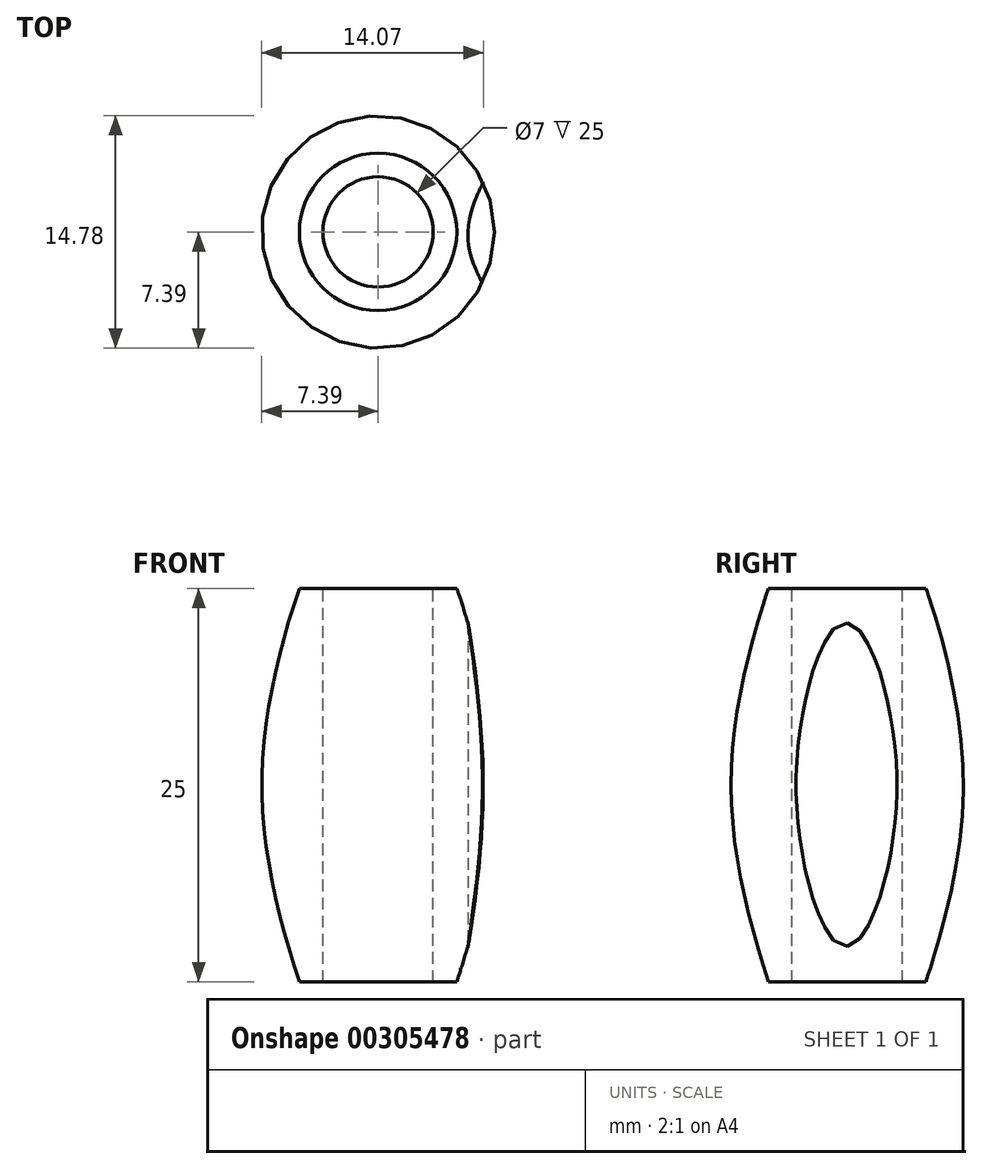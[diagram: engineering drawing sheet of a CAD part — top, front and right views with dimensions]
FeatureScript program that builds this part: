
annotation { "Feature Type Name" : "Feature", "Feature Type Description" : "" }
export const myFeature = defineFeature(function(context is Context, id is Id, definition is map)
    precondition{}
    {
        {
            var Q0;
            Q0=qCreatedBy(makeId("Front.planeOp"),FACE);
            var sketch = newSketch(context, id + "F0", { "sketchPlane" : qUnion([Q0])});
            skLineSegment(sketch, "E0", {"start": v(0, 12.5) * mm, "end": v(5, 12.5) * mm});
            skFitSpline(sketch, "E1", {"points": [v(5, 12.5) * mm, v(7.39, 0) * mm, v(5, -12.5) * mm], "startDerivative": vector(2.03, -6.1) * mm, "endDerivative": vector(-1.99, -6.8) * mm});
            skLineSegment(sketch, "E2", {"start": v(5, -12.5) * mm, "end": v(0, -12.5) * mm});
            skLineSegment(sketch, "E3", {"start": v(0, 12.5) * mm, "end": v(0, -12.5) * mm, "construction": true});
            skLineSegment(sketch, "E4", {"start": v(0, 0) * mm, "end": v(4.35, 0) * mm, "construction": true});
            skLineSegment(sketch, "E5", {"start": v(3.5, 12.5) * mm, "end": v(3.5, -12.5) * mm});
            skSolve(sketch);
        }
        {
            var Q0;
            {var subQ0=sQuery(id+"F0.wireOp",EDGE,"E1");Q0=makeQuery(id+"F0.imprint","IMPRINT",FACE,{"disambiguationData":[TD([[makeQuery(id+"F0.imprint","IMPRINT",EDGE,{"derivedFrom":subQ0}),-1.0]])]});}
            var Q1;
            Q1=sQuery(id+"F0.wireOp",EDGE,"E3");
            revolve(context, id + "F1", {"entities" : qUnion([Q0]), "axis" : qUnion([Q1]), "revolveType" : RevolveType.FULL});
        }
        {
            var Q0;
            Q0=qCreatedBy(makeId("Top.planeOp"),FACE);
            var sketch = newSketch(context, id + "F2", { "sketchPlane" : qUnion([Q0])});
            skFitSpline(sketch, "E6", {"points": [v(8.27, 6.1) * mm, v(5.7, 0) * mm, v(8.6, -6.4) * mm], "startDerivative": vector(-6.47, -12.33) * mm, "endDerivative": vector(9.46, -14.56) * mm});
            skLineSegment(sketch, "E7", {"start": v(8.27, 6.1) * mm, "end": v(8.6, -6.4) * mm});
            skSolve(sketch);
        }
        {
            var Q0;
            Q0 = qSketchRegion(id + "F2", true);
            extrude(context, id + "F3", {"entities" : qUnion([Q0]), "operationType" : NewBodyOperationType.REMOVE, "oppositeDirection" : true, "depth" : 25 * mm, "hasSecondDirection" : true, "secondDirectionOppositeDirection" : false, "secondDirectionDepth" : 25 * mm});
        }
    });
